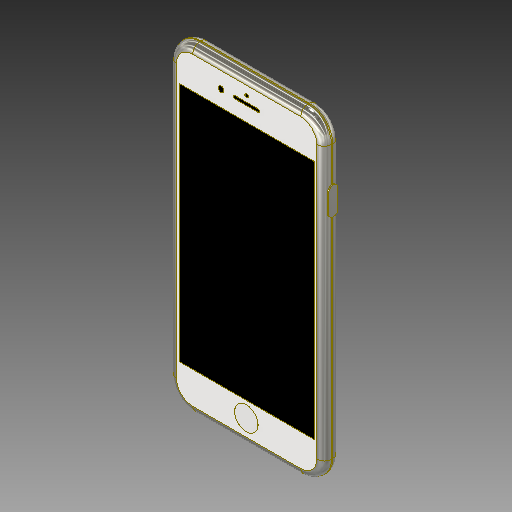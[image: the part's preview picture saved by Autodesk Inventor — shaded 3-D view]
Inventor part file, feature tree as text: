
AUTODESK INVENTOR PART (.ipt)
format: ipt  version: 2019 (Build 230136000, 136)  size: 415,232 bytes
history: native  units: in
note: dims shown in document units (in); Inventor stores cm internally (conversion verified against a paired STEP export)
features: extrude x10, sketch x10, fillet x1
ambient origin geometry x8: Origin, YZ Plane, XZ Plane, XY Plane, X Axis, Y Axis, Z Axis, Center Point
bodies: Solid1 (feature_tree)
feature tree (21):
  extrude  "Extrusion1"  Depth=5.44in
  fillet  "Fillet1"  Radius=0.4in
  extrude  "Extrusion2"  Depth=4.1in
  extrude  "Extrusion3"  Depth=0.17in
  extrude  "Extrusion4"  Depth=0.125in
  extrude  "Extrusion5"  Depth=2.3in
  extrude  "Extrusion6"  Depth=0.17in
  extrude  "Extrusion7"  Depth=0.4in
  extrude  "Extrusion8"  Depth=0.001in TaperAngle=0.0deg
  extrude  "Extrusion9"  Depth=0.4in
  extrude  "Extrusion10"  Depth=0.16in
  sketch  "Sketch1"  dims[d0=2.64in d1=5.44in d2=0.4in]
  sketch  "Sketch2"  dims[d3=2.3in d4=4.1in]
  sketch  "Sketch3"  dims[d5=0.67in d6=0.17in]
  sketch  "Sketch4"  dims[d7=0.27in d8=0.0in d9=0.125in]
  sketch  "Sketch5"  dims[d10=4.1in d11=2.3in]
  sketch  "Sketch6"  dims[d12=0.67in d13=0.17in]
  sketch  "Sketch7"  dims[d14=0.001in d15=0.0in d16=0.4in]
  sketch  "Sketch8"  dims[d17=1.2in d18=0.001in d19=0.0in]
  sketch  "Sketch9"  dims[d20=0.05in d21=0.4in]
  sketch  "Sketch10"  dims[d22=0.1in d23=0.16in d24=0.06in d25=0.0975in d26=0.001in d27=0.0in d28=0.25in d29=0.4375in d30=0.1875in d31=0.05in d32=-0.0687in d33=0.0394in d34=0.1575in d35=0.3125in d36=0.3125in d37=0.25in d38=0.25in d39=0.001in d40=0.0in d41=0.315in d42=0.0787in d43=0.6693in d44=0.02in d45=0.0in d46=0.0591in d47=0.0787in d48=0.1575in d49=0.1575in d50=0.315in d51=0.7874in d52=0.01in d53=0.0in d54=0.0295in d55=0.1969in d58=0.0in d59=0.03in d60=0.0in d61=0.291in d62=0.01in d63=0.01in d64=0.01in d65=0.01in d66=0.01in d67=0.01in d68=0.7in d69=0.0in]
